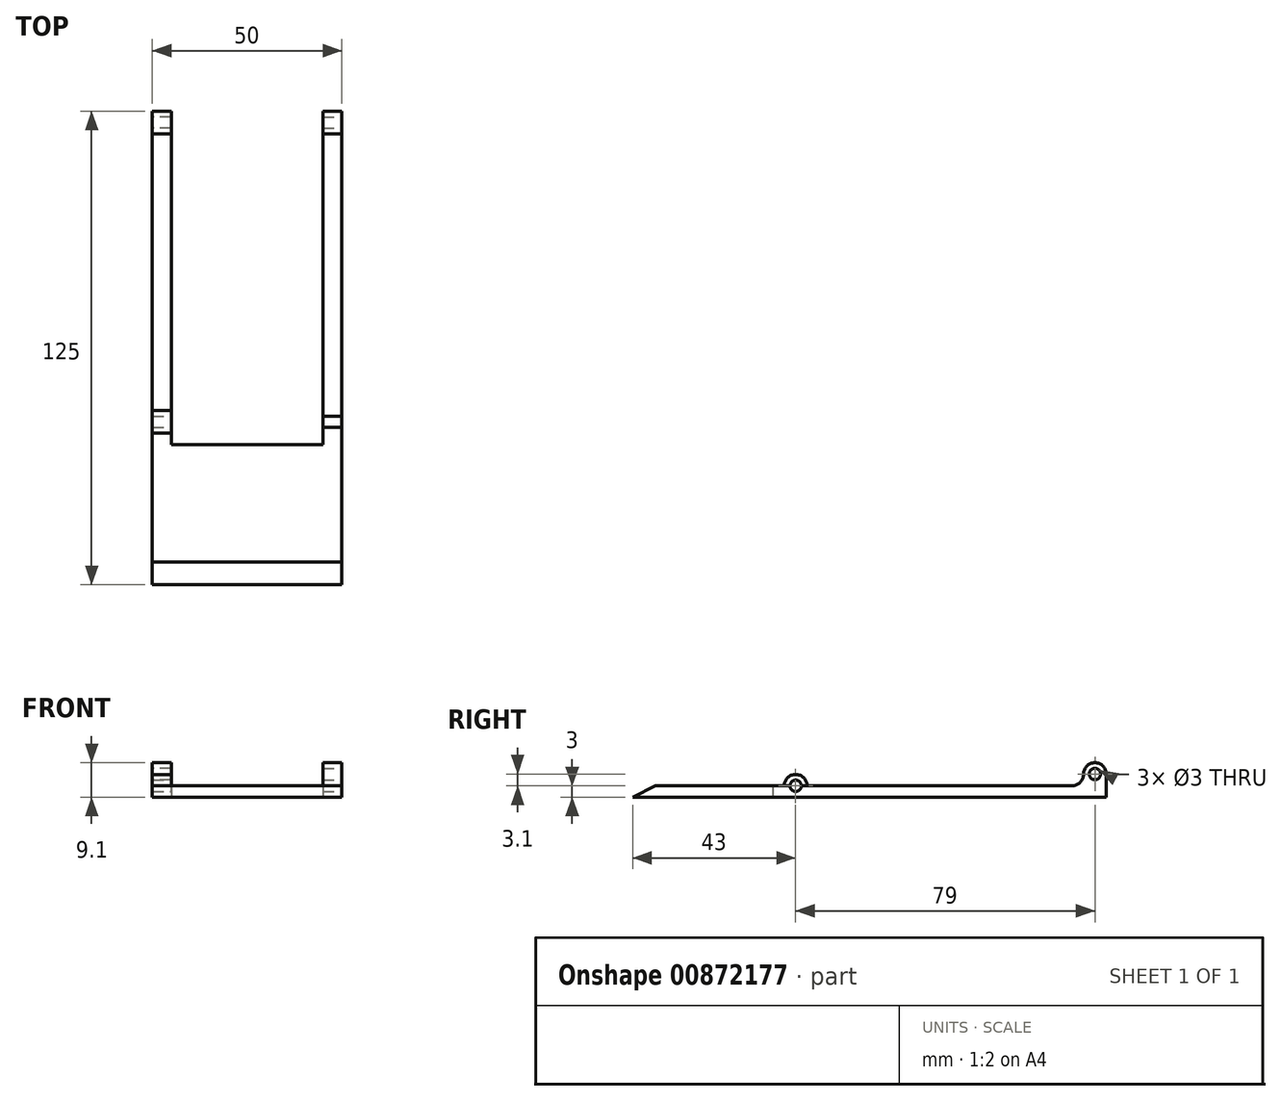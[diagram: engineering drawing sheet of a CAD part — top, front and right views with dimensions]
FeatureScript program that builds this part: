
annotation { "Feature Type Name" : "Feature", "Feature Type Description" : "" }
export const myFeature = defineFeature(function(context is Context, id is Id, definition is map)
    precondition{}
    {
        {
            var Q0;
            Q0=qCreatedBy(makeId("Top.planeOp"),FACE);
            var sketch = newSketch(context, id + "F0", { "sketchPlane" : qUnion([Q0])});
            skLineSegment(sketch, "E0.bottom", {"start": v(-25, 62.5) * mm, "end": v(25, 62.5) * mm});
            skLineSegment(sketch, "E0.top", {"start": v(-25, -62.5) * mm, "end": v(25, -62.5) * mm});
            skLineSegment(sketch, "E0.left", {"start": v(-25, 62.5) * mm, "end": v(-25, -62.5) * mm});
            skLineSegment(sketch, "E0.right", {"start": v(25, 62.5) * mm, "end": v(25, -62.5) * mm});
            skPoint(sketch, "E0.middle", {"position": v(0, 0) * mm});
            skLineSegment(sketch, "E1.bottom", {"start": v(-20, 62.5) * mm, "end": v(20, 62.5) * mm});
            skLineSegment(sketch, "E1.top", {"start": v(-20, -25.5) * mm, "end": v(20, -25.5) * mm});
            skLineSegment(sketch, "E1.left", {"start": v(-20, 62.5) * mm, "end": v(-20, -25.5) * mm});
            skLineSegment(sketch, "E1.right", {"start": v(20, 62.5) * mm, "end": v(20, -25.5) * mm});
            skSolve(sketch);
        }
        {
            var Q0;
            Q0=makeQuery(id+"F0.imprint","IMPRINT",FACE,{"disambiguationData":[TD([[makeQuery(id+"F0.imprint","IMPRINT",EDGE,{"derivedFrom":sQuery(id+"F0.wireOp",EDGE,"E0.top")}),1.0]])]});
            extrude(context, id + "F1", {"entities" : qUnion([Q0]), "depth" : 3 * mm, "offsetDistance" : 25 * mm});
        }
        {
            var Q0;
            Q0=makeQuery(id+"F1.opExtrude","SWEPT_FACE",FACE,{"disambiguationData":[OSD([sQuery(id+"F0.wireOp",EDGE,"E0.right")])]});
            var sketch = newSketch(context, id + "F2", { "sketchPlane" : qUnion([Q0])});
            skCircle(sketch, "E2", {"center": v(-19.5, 3) * mm, "radius": 3 * mm});
            skSolve(sketch);
        }
        {
            var Q0;
            {var subQ0=sQuery(id+"F2.wireOp",EDGE,"E2");var subQ1=makeQuery(id+"F1.opExtrude","CAP_EDGE",EDGE,{"disambiguationData":[OSD([sQuery(id+"F0.wireOp",EDGE,"E0.right")])],"isStart":false});var subQ2=makeQuery(id+"F2.imprint","INTERSECT",VERTEX,{"disambiguationData":[OD(0.0)],"derivedFrom":[subQ1,subQ0]});Q0=makeQuery(id+"F2.imprint","IMPRINT",FACE,{"disambiguationData":[TD([[makeQuery(id+"F2.imprint","IMPRINT",EDGE,{"disambiguationData":[TD([[subQ2,1.0]])],"derivedFrom":subQ0}),1.0]])]});}
            extrude(context, id + "F3", {"entities" : qUnion([Q0]), "oppositeDirection" : true, "depth" : 5 * mm, "offsetDistance" : 25 * mm});
        }
        {
            var Q0;
            Q0=makeQuery(id+"F1.opExtrude","SWEPT_FACE",FACE,{"disambiguationData":[OSD([sQuery(id+"F0.wireOp",EDGE,"E0.left")])]});
            var sketch = newSketch(context, id + "F4", { "sketchPlane" : qUnion([Q0])});
            skCircle(sketch, "E3", {"center": v(19.5, 3) * mm, "radius": 3 * mm});
            skSolve(sketch);
        }
        {
            var Q0;
            {var subQ0=sQuery(id+"F4.wireOp",EDGE,"E3");var subQ1=makeQuery(id+"F1.opExtrude","CAP_EDGE",EDGE,{"disambiguationData":[OSD([sQuery(id+"F0.wireOp",EDGE,"E0.left")])],"isStart":false});var subQ2=makeQuery(id+"F4.imprint","INTERSECT",VERTEX,{"disambiguationData":[OD(0.0)],"derivedFrom":[subQ1,subQ0]});Q0=makeQuery(id+"F4.imprint","IMPRINT",FACE,{"disambiguationData":[TD([[makeQuery(id+"F4.imprint","IMPRINT",EDGE,{"disambiguationData":[TD([[subQ2,1.0]])],"derivedFrom":subQ0}),1.0]])]});}
            extrude(context, id + "F5", {"entities" : qUnion([Q0]), "oppositeDirection" : true, "depth" : 5 * mm, "offsetDistance" : 25 * mm});
        }
        {
            var Q0;
            Q0=makeQuery(id+"F1.opExtrude","SWEPT_FACE",FACE,{"disambiguationData":[OSD([sQuery(id+"F0.wireOp",EDGE,"E0.left")])]});
            var sketch = newSketch(context, id + "F6", { "sketchPlane" : qUnion([Q0])});
            skLineSegment(sketch, "E4.bottom", {"start": v(-62.5, 3) * mm, "end": v(-56.5, 3) * mm});
            skLineSegment(sketch, "E4.top", {"start": v(-62.5, 6.1) * mm, "end": v(-56.5, 6.1) * mm});
            skLineSegment(sketch, "E4.left", {"start": v(-62.5, 3) * mm, "end": v(-62.5, 6.1) * mm});
            skLineSegment(sketch, "E4.right", {"start": v(-56.5, 3) * mm, "end": v(-56.5, 6.1) * mm});
            skCircle(sketch, "E5", {"center": v(-59.5, 6.1) * mm, "radius": 3 * mm});
            skCircle(sketch, "E6", {"center": v(-53.4, 6.1) * mm, "radius": 3.1 * mm});
            skCircle(sketch, "E7", {"center": v(-59.5, 6.1) * mm, "radius": 1.5 * mm});
            skSolve(sketch);
        }
        {
            var Q0;
            {var subQ0=sQuery(id+"F6.wireOp",EDGE,"E5");var subQ3=sQuery(id+"F6.wireOp",EDGE,"E4.bottom");var subQ4=makeQuery(id+"F6.imprint","INTERSECT",VERTEX,{"disambiguationData":[OD(0.0)],"derivedFrom":[subQ3,subQ0]});Q0=makeQuery(id+"F6.imprint","IMPRINT",FACE,{"disambiguationData":[TD([[makeQuery(id+"F6.imprint","IMPRINT",EDGE,{"disambiguationData":[TD([[subQ4,-1.0]])],"derivedFrom":subQ3}),1.0]])]});}
            var Q1;
            {var subQ0=sQuery(id+"F6.wireOp",EDGE,"E4.right");Q1=makeQuery(id+"F6.imprint","IMPRINT",FACE,{"disambiguationData":[TD([[makeQuery(id+"F6.imprint","IMPRINT",EDGE,{"derivedFrom":subQ0}),1.0]])]});}
            var Q2;
            {var subQ1=sQuery(id+"F6.wireOp",EDGE,"E4.top");var subQ3=sQuery(id+"F6.wireOp",EDGE,"E7");var subQ4=makeQuery(id+"F6.imprint","INTERSECT",VERTEX,{"disambiguationData":[OD(0.0)],"derivedFrom":[subQ1,subQ3]});Q2=makeQuery(id+"F6.imprint","IMPRINT",FACE,{"disambiguationData":[TD([[makeQuery(id+"F6.imprint","IMPRINT",EDGE,{"disambiguationData":[TD([[subQ4,1.0]])],"derivedFrom":subQ3}),-1.0]])]});}
            var Q3;
            {var subQ0=sQuery(id+"F6.wireOp",EDGE,"E4.right");Q3=makeQuery(id+"F6.imprint","IMPRINT",FACE,{"disambiguationData":[TD([[makeQuery(id+"F6.imprint","IMPRINT",EDGE,{"derivedFrom":subQ0}),-1.0]])]});}
            var Q4;
            {var subQ0=sQuery(id+"F6.wireOp",EDGE,"E4.left");Q4=makeQuery(id+"F6.imprint","IMPRINT",FACE,{"disambiguationData":[TD([[makeQuery(id+"F6.imprint","IMPRINT",EDGE,{"derivedFrom":subQ0}),-1.0]])]});}
            var Q5;
            {var subQ1=sQuery(id+"F6.wireOp",EDGE,"E4.top");var subQ3=sQuery(id+"F6.wireOp",EDGE,"E7");var subQ4=makeQuery(id+"F6.imprint","INTERSECT",VERTEX,{"disambiguationData":[OD(0.0)],"derivedFrom":[subQ1,subQ3]});Q5=makeQuery(id+"F6.imprint","IMPRINT",FACE,{"disambiguationData":[TD([[makeQuery(id+"F6.imprint","IMPRINT",EDGE,{"disambiguationData":[TD([[subQ4,-1.0]])],"derivedFrom":subQ3}),-1.0]])]});}
            extrude(context, id + "F7", {"entities" : qUnion([Q0, Q1, Q2, Q3, Q4, Q5]), "operationType" : NewBodyOperationType.ADD, "oppositeDirection" : true, "depth" : 5 * mm, "offsetDistance" : 25 * mm});
        }
        {
            var Q0;
            Q0=makeQuery(id+"F1.opExtrude","SWEPT_FACE",FACE,{"disambiguationData":[OSD([sQuery(id+"F0.wireOp",EDGE,"E0.right")])]});
            var sketch = newSketch(context, id + "F8", { "sketchPlane" : qUnion([Q0])});
            skLineSegment(sketch, "E8.bottom", {"start": v(62.5, 3) * mm, "end": v(56.5, 3) * mm});
            skLineSegment(sketch, "E8.top", {"start": v(62.5, 6.1) * mm, "end": v(56.5, 6.1) * mm});
            skLineSegment(sketch, "E8.left", {"start": v(62.5, 3) * mm, "end": v(62.5, 6.1) * mm});
            skLineSegment(sketch, "E8.right", {"start": v(56.5, 3) * mm, "end": v(56.5, 6.1) * mm});
            skCircle(sketch, "E9", {"center": v(59.5, 6.1) * mm, "radius": 3 * mm});
            skCircle(sketch, "E10", {"center": v(59.5, 6.1) * mm, "radius": 1.5 * mm});
            skCircle(sketch, "E11", {"center": v(53.4, 6.1) * mm, "radius": 3.1 * mm});
            skSolve(sketch);
        }
        {
            var Q0;
            {var subQ0=sQuery(id+"F8.wireOp",EDGE,"E9");var subQ3=sQuery(id+"F8.wireOp",EDGE,"E8.bottom");var subQ9=makeQuery(id+"F8.imprint","INTERSECT",VERTEX,{"disambiguationData":[OD(0.0)],"derivedFrom":[subQ3,subQ0]});Q0=makeQuery(id+"F8.imprint","IMPRINT",FACE,{"disambiguationData":[TD([[makeQuery(id+"F8.imprint","IMPRINT",EDGE,{"disambiguationData":[TD([[subQ9,-1.0]])],"derivedFrom":subQ3}),-1.0]])]});}
            var Q1;
            {var subQ1=sQuery(id+"F8.wireOp",EDGE,"E8.top");var subQ3=sQuery(id+"F8.wireOp",EDGE,"E10");var subQ4=makeQuery(id+"F8.imprint","INTERSECT",VERTEX,{"disambiguationData":[OD(0.0)],"derivedFrom":[subQ1,subQ3]});Q1=makeQuery(id+"F8.imprint","IMPRINT",FACE,{"disambiguationData":[TD([[makeQuery(id+"F8.imprint","IMPRINT",EDGE,{"disambiguationData":[TD([[subQ4,-1.0]])],"derivedFrom":subQ3}),-1.0]])]});}
            var Q2;
            {var subQ0=sQuery(id+"F8.wireOp",EDGE,"E8.right");Q2=makeQuery(id+"F8.imprint","IMPRINT",FACE,{"disambiguationData":[TD([[makeQuery(id+"F8.imprint","IMPRINT",EDGE,{"derivedFrom":subQ0}),-1.0]])]});}
            var Q3;
            {var subQ0=sQuery(id+"F8.wireOp",EDGE,"E8.right");Q3=makeQuery(id+"F8.imprint","IMPRINT",FACE,{"disambiguationData":[TD([[makeQuery(id+"F8.imprint","IMPRINT",EDGE,{"derivedFrom":subQ0}),1.0]])]});}
            var Q4;
            {var subQ0=sQuery(id+"F8.wireOp",EDGE,"E8.left");Q4=makeQuery(id+"F8.imprint","IMPRINT",FACE,{"disambiguationData":[TD([[makeQuery(id+"F8.imprint","IMPRINT",EDGE,{"derivedFrom":subQ0}),1.0]])]});}
            var Q5;
            {var subQ1=sQuery(id+"F8.wireOp",EDGE,"E8.top");var subQ3=sQuery(id+"F8.wireOp",EDGE,"E10");var subQ4=makeQuery(id+"F8.imprint","INTERSECT",VERTEX,{"disambiguationData":[OD(0.0)],"derivedFrom":[subQ1,subQ3]});Q5=makeQuery(id+"F8.imprint","IMPRINT",FACE,{"disambiguationData":[TD([[makeQuery(id+"F8.imprint","IMPRINT",EDGE,{"disambiguationData":[TD([[subQ4,1.0]])],"derivedFrom":subQ3}),-1.0]])]});}
            extrude(context, id + "F9", {"entities" : qUnion([Q0, Q1, Q2, Q3, Q4, Q5]), "oppositeDirection" : true, "depth" : 5 * mm, "offsetDistance" : 25 * mm});
        }
        {
            var Q0;
            Q0=makeQuery(id+"F1.opExtrude","SWEPT_BODY",BODY,{"disambiguationData":[OSD([sQuery(id+"F0.wireOp",EDGE,"E0.bottom"),sQuery(id+"F0.wireOp",EDGE,"E0.top"),sQuery(id+"F0.wireOp",EDGE,"E0.left"),sQuery(id+"F0.wireOp",EDGE,"E0.right"),sQuery(id+"F0.wireOp",EDGE,"E1.top"),sQuery(id+"F0.wireOp",EDGE,"E1.left"),sQuery(id+"F0.wireOp",EDGE,"E1.right")])]});
            var Q1;
            Q1=makeQuery(id+"F3.opExtrude","SWEPT_BODY",BODY,{"disambiguationData":[OSD([sQuery(id+"F0.wireOp",EDGE,"E0.right"),sQuery(id+"F2.wireOp",EDGE,"E2")])]});
            var Q2;
            Q2=makeQuery(id+"F5.opExtrude","SWEPT_BODY",BODY,{"disambiguationData":[OSD([sQuery(id+"F0.wireOp",EDGE,"E0.left"),sQuery(id+"F4.wireOp",EDGE,"E3")])]});
            var Q3;
            Q3=makeQuery(id+"F9.opExtrude","SWEPT_BODY",BODY,{"disambiguationData":[OSD([sQuery(id+"F0.wireOp",EDGE,"E0.right"),sQuery(id+"F8.wireOp",EDGE,"E8.bottom"),sQuery(id+"F8.wireOp",EDGE,"E8.left"),sQuery(id+"F8.wireOp",EDGE,"E9"),sQuery(id+"F8.wireOp",EDGE,"E10"),sQuery(id+"F8.wireOp",EDGE,"E11")])]});
            booleanBodies(context, id + "F10", {"operationType" : BooleanOperationType.UNION, "tools" : qUnion([Q0, Q1, Q2, Q3])});
        }
        {
            var Q0;
            {var subQ0=sQuery(id+"F0.wireOp",EDGE,"E0.right");Q0=makeQuery(id+"F10.opBoolean","MERGE",FACE,{"derivedFrom":[makeQuery(id+"F1.opExtrude","SWEPT_FACE",FACE,{"disambiguationData":[OSD([subQ0])]}),makeQuery(id+"F3.opExtrude","CAP_FACE",FACE,{"disambiguationData":[OSD([subQ0,sQuery(id+"F2.wireOp",EDGE,"E2")])],"isStart":true}),makeQuery(id+"F9.opExtrude","CAP_FACE",FACE,{"disambiguationData":[OSD([subQ0,sQuery(id+"F8.wireOp",EDGE,"E8.bottom"),sQuery(id+"F8.wireOp",EDGE,"E8.left"),sQuery(id+"F8.wireOp",EDGE,"E9"),sQuery(id+"F8.wireOp",EDGE,"E10"),sQuery(id+"F8.wireOp",EDGE,"E11")])],"isStart":true})]});}
            var sketch = newSketch(context, id + "F11", { "sketchPlane" : qUnion([Q0])});
            skCircle(sketch, "E12", {"center": v(-19.5, 3) * mm, "radius": 1.5 * mm});
            skSolve(sketch);
        }
        {
            var Q0;
            Q0=makeQuery(id+"F11.imprint","IMPRINT",FACE,{"disambiguationData":[TD([[makeQuery(id+"F11.imprint","IMPRINT",EDGE,{"derivedFrom":sQuery(id+"F11.wireOp",EDGE,"E12")}),1.0]])]});
            extrude(context, id + "F12", {"entities" : qUnion([Q0]), "operationType" : NewBodyOperationType.REMOVE, "oppositeDirection" : true, "depth" : 55 * mm, "offsetDistance" : 25 * mm});
        }
        {
            var Q0;
            {var subQ0=sQuery(id+"F0.wireOp",EDGE,"E0.right");Q0=makeQuery(id+"F10.opBoolean","MERGE",FACE,{"derivedFrom":[makeQuery(id+"F1.opExtrude","SWEPT_FACE",FACE,{"disambiguationData":[OSD([subQ0])]}),makeQuery(id+"F3.opExtrude","CAP_FACE",FACE,{"disambiguationData":[OSD([subQ0,sQuery(id+"F2.wireOp",EDGE,"E2")])],"isStart":true}),makeQuery(id+"F9.opExtrude","CAP_FACE",FACE,{"disambiguationData":[OSD([subQ0,sQuery(id+"F8.wireOp",EDGE,"E8.bottom"),sQuery(id+"F8.wireOp",EDGE,"E8.left"),sQuery(id+"F8.wireOp",EDGE,"E9"),sQuery(id+"F8.wireOp",EDGE,"E10"),sQuery(id+"F8.wireOp",EDGE,"E11")])],"isStart":true})]});}
            var sketch = newSketch(context, id + "F13", { "sketchPlane" : qUnion([Q0])});
            skLineSegment(sketch, "E13", {"start": v(-62.5, 0) * mm, "end": v(-56.5, 3) * mm});
            skSolve(sketch);
        }
        {
            var Q0;
            {var subQ0=sQuery(id+"F13.wireOp",EDGE,"E13");Q0=makeQuery(id+"F13.imprint","IMPRINT",FACE,{"disambiguationData":[TD([[makeQuery(id+"F13.imprint","IMPRINT",EDGE,{"derivedFrom":subQ0}),1.0]])]});}
            extrude(context, id + "F14", {"entities" : qUnion([Q0]), "operationType" : NewBodyOperationType.REMOVE, "oppositeDirection" : true, "depth" : 100 * mm, "offsetDistance" : 25 * mm});
        }
    });
